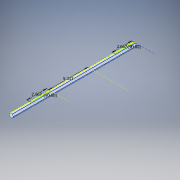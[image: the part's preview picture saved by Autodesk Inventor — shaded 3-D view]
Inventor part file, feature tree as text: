
AUTODESK INVENTOR PART (.ipt)
format: ipt  version: 2017 (Build 210142000, 142)  size: 149,504 bytes
history: native  units: in
note: dims shown in document units (in); Inventor stores cm internally (conversion verified against a paired STEP export)
features: sketch x5, split x1, fillet x1
ambient origin geometry x8: Origin, YZ Plane, XZ Plane, XY Plane, X Axis, Y Axis, Z Axis, Center Point
bodies: Solid1 (feature_tree)
feature tree (7):
  sketch  "Sketch1"  dims[d5=5.333in]
  split  "Split1"
  sketch  "Sketch3"  dims[d8=90.0deg]
  sketch  "Sketch4"  dims[d9=2.6665in]
  sketch  "Sketch5"  dims[d10=90.0deg d11=16.75in]
  sketch  "Sketch2"  dims[d7=2.6665in]
  fillet  "Fillet1"  Radius=8.5in
